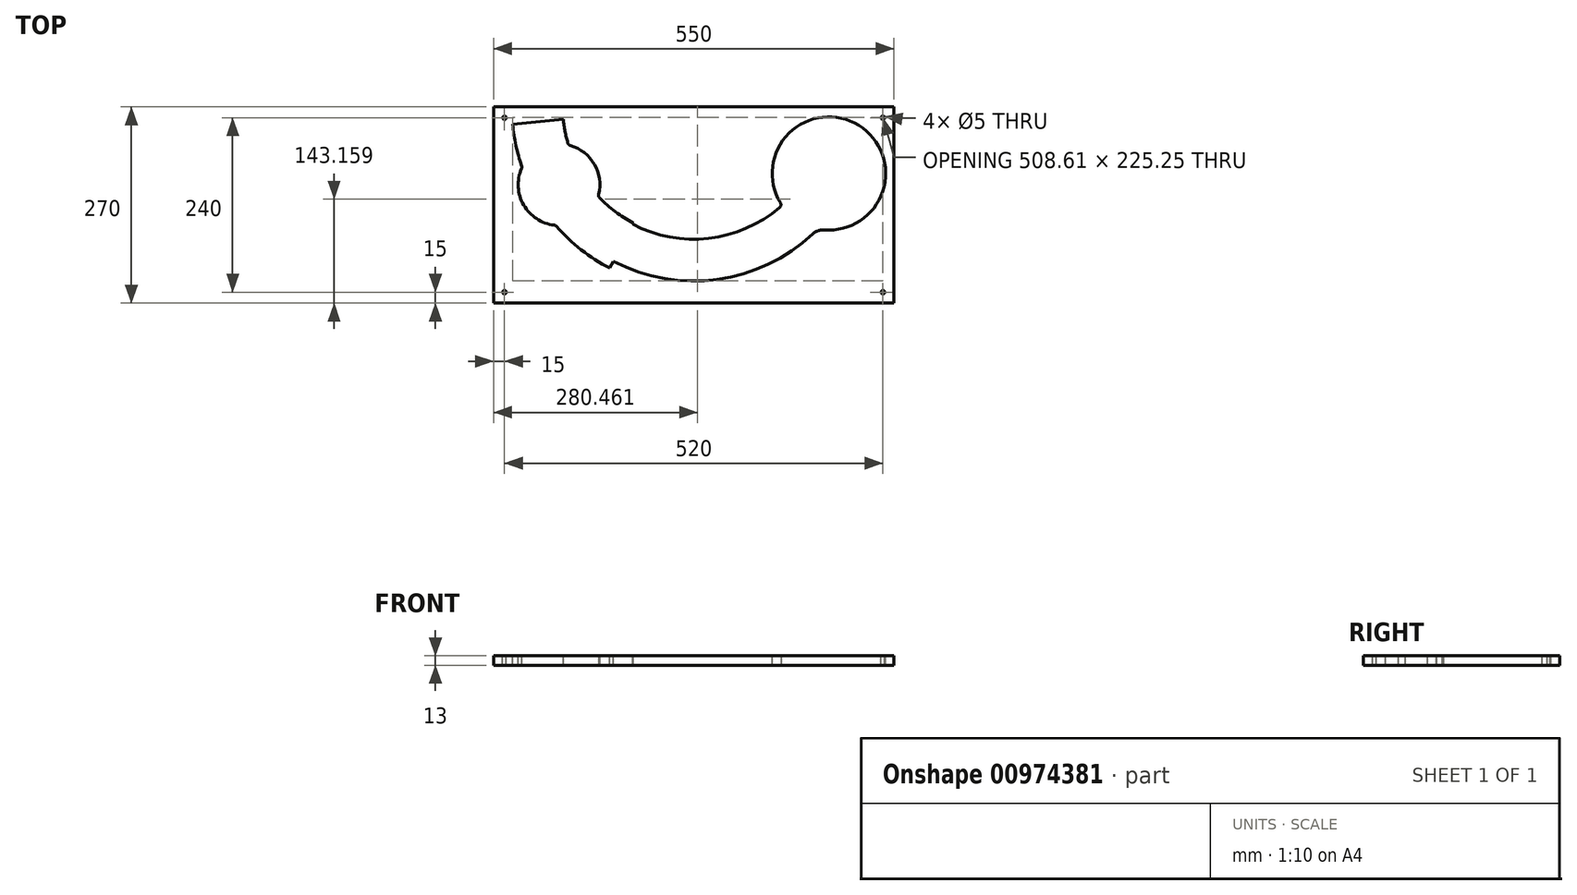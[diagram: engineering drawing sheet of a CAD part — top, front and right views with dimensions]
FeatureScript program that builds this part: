
annotation { "Feature Type Name" : "Feature", "Feature Type Description" : "" }
export const myFeature = defineFeature(function(context is Context, id is Id, definition is map)
    precondition{}
    {
        {
            var Q0;
            Q0=qCreatedBy(makeId("Top.planeOp"),FACE);
            var sketch = newSketch(context, id + "F0", { "sketchPlane" : qUnion([Q0])});
            skLineSegment(sketch, "E0.bottom", {"start": v(0, 0) * mm, "end": v(550, 0) * mm});
            skLineSegment(sketch, "E0.top", {"start": v(0, -270) * mm, "end": v(550, -270) * mm});
            skLineSegment(sketch, "E0.left", {"start": v(0, 0) * mm, "end": v(0, -270) * mm});
            skLineSegment(sketch, "E0.right", {"start": v(550, 0) * mm, "end": v(550, -270) * mm});
            skSolve(sketch);
        }
        {
            var Q0;
            Q0=makeQuery(id+"F0.imprint","IMPRINT",FACE,{"disambiguationData":[TD([[makeQuery(id+"F0.imprint","IMPRINT",EDGE,{"derivedFrom":sQuery(id+"F0.wireOp",EDGE,"E0.bottom")}),-1.0]])]});
            extrude(context, id + "F1", {"entities" : qUnion([Q0]), "oppositeDirection" : true, "depth" : 13 * mm, "offsetDistance" : 25 * mm});
        }
        {
            var Q0;
            Q0=makeQuery(id+"F1.opExtrude","CAP_FACE",FACE,{"disambiguationData":[OSD([sQuery(id+"F0.wireOp",EDGE,"E0.bottom"),sQuery(id+"F0.wireOp",EDGE,"E0.top"),sQuery(id+"F0.wireOp",EDGE,"E0.left"),sQuery(id+"F0.wireOp",EDGE,"E0.right")])],"isStart":true});
            var sketch = newSketch(context, id + "F2", { "sketchPlane" : qUnion([Q0])});
            skArc(sketch, "E1", {"start": v(26.15, -24) * mm, "mid": v(195.26, -236.94) * mm, "end": v(458.7, -169.57) * mm});
            skArc(sketch, "E2", {"start": v(95.83, -17.28) * mm, "mid": v(209.67, -167.73) * mm, "end": v(395.28, -133.91) * mm});
            skPoint(sketch, "E3.start.orphan", {"position": v(275, -180) * mm});
            skCircle(sketch, "E4", {"center": v(460.77, -91.66) * mm, "radius": 77.94 * mm});
            skLineSegment(sketch, "E5", {"start": v(95.83, -17.28) * mm, "end": v(26.15, -24) * mm});
            skLineSegment(sketch, "E6", {"start": v(191.91, -159.67) * mm, "end": v(159.6, -221.77) * mm});
            skLineSegment(sketch, "E7", {"start": v(550, 0) * mm, "end": v(535, 0) * mm});
            skLineSegment(sketch, "E8", {"start": v(535, 0) * mm, "end": v(535, -15) * mm});
            skLineSegment(sketch, "E9", {"start": v(0, -270) * mm, "end": v(15, -270) * mm});
            skLineSegment(sketch, "E10", {"start": v(15, -270) * mm, "end": v(15, -255) * mm});
            skCircle(sketch, "E11", {"center": v(15, -255) * mm, "radius": 2.5 * mm});
            skCircle(sketch, "E12", {"center": v(535, -255) * mm, "radius": 2.5 * mm});
            skCircle(sketch, "E13", {"center": v(535, -15) * mm, "radius": 2.5 * mm});
            skCircle(sketch, "E14", {"center": v(15, -15) * mm, "radius": 2.5 * mm});
            skCircle(sketch, "E15", {"center": v(89.9, -107.02) * mm, "radius": 56.06 * mm});
            skCircle(sketch, "E16", {"center": v(275, 0) * mm, "radius": 182 * mm});
            skCircle(sketch, "E17", {"center": v(275, 0) * mm, "radius": 239.5 * mm});
            skSolve(sketch);
        }
        {
            var Q0;
            {var subQ0=sQuery(id+"F2.wireOp",EDGE,"E15");var subQ1=sQuery(id+"F2.wireOp",EDGE,"E2");var subQ2=makeQuery(id+"F2.imprint","INTERSECT",VERTEX,{"disambiguationData":[OD(0.0)],"derivedFrom":[subQ1,subQ0]});Q0=makeQuery(id+"F2.imprint","IMPRINT",FACE,{"disambiguationData":[TD([[makeQuery(id+"F2.imprint","IMPRINT",EDGE,{"disambiguationData":[TD([[subQ2,-1.0]])],"derivedFrom":subQ1}),1.0]])]});}
            var Q1;
            {var subQ0=sQuery(id+"F2.wireOp",EDGE,"E16");var subQ1=sQuery(id+"F2.wireOp",EDGE,"E15");var subQ2=makeQuery(id+"F2.imprint","INTERSECT",VERTEX,{"disambiguationData":[OD(0.0)],"derivedFrom":[subQ1,subQ0]});Q1=makeQuery(id+"F2.imprint","IMPRINT",FACE,{"disambiguationData":[TD([[makeQuery(id+"F2.imprint","IMPRINT",EDGE,{"disambiguationData":[TD([[subQ2,-1.0]])],"derivedFrom":subQ1}),1.0]])]});}
            var Q2;
            {var subQ0=sQuery(id+"F2.wireOp",EDGE,"E16");var subQ1=sQuery(id+"F2.wireOp",EDGE,"E5");var subQ2=makeQuery(id+"F2.imprint","INTERSECT",VERTEX,{"derivedFrom":[subQ1,subQ0]});Q2=makeQuery(id+"F2.imprint","IMPRINT",FACE,{"disambiguationData":[TD([[makeQuery(id+"F2.imprint","IMPRINT",EDGE,{"disambiguationData":[TD([[subQ2,-1.0]])],"derivedFrom":subQ1}),1.0]])]});}
            var Q3;
            {var subQ0=sQuery(id+"F2.wireOp",EDGE,"E5");var subQ1=sQuery(id+"F2.wireOp",EDGE,"E1");var subQ2=makeQuery(id+"F2.imprint","INTERSECT",VERTEX,{"derivedFrom":[subQ1,subQ0]});Q3=makeQuery(id+"F2.imprint","IMPRINT",FACE,{"disambiguationData":[TD([[makeQuery(id+"F2.imprint","IMPRINT",EDGE,{"disambiguationData":[TD([[subQ2,-1.0]])],"derivedFrom":subQ1}),1.0]])]});}
            var Q4;
            {var subQ0=sQuery(id+"F2.wireOp",EDGE,"E15");var subQ1=sQuery(id+"F2.wireOp",EDGE,"E1");var subQ2=makeQuery(id+"F2.imprint","INTERSECT",VERTEX,{"disambiguationData":[OD(0.0)],"derivedFrom":[subQ1,subQ0]});Q4=makeQuery(id+"F2.imprint","IMPRINT",FACE,{"disambiguationData":[TD([[makeQuery(id+"F2.imprint","IMPRINT",EDGE,{"disambiguationData":[TD([[subQ2,-1.0]])],"derivedFrom":subQ1}),1.0]])]});}
            var Q5;
            {var subQ0=sQuery(id+"F2.wireOp",EDGE,"E15");var subQ1=sQuery(id+"F2.wireOp",EDGE,"E1");var subQ2=makeQuery(id+"F2.imprint","INTERSECT",VERTEX,{"disambiguationData":[OD(0.0)],"derivedFrom":[subQ1,subQ0]});Q5=makeQuery(id+"F2.imprint","IMPRINT",FACE,{"disambiguationData":[TD([[makeQuery(id+"F2.imprint","IMPRINT",EDGE,{"disambiguationData":[TD([[subQ2,-1.0]])],"derivedFrom":subQ1}),-1.0]])]});}
            var Q6;
            {var subQ0=sQuery(id+"F2.wireOp",EDGE,"E16");var subQ1=sQuery(id+"F2.wireOp",EDGE,"E6");var subQ2=makeQuery(id+"F2.imprint","INTERSECT",VERTEX,{"derivedFrom":[subQ1,subQ0]});Q6=makeQuery(id+"F2.imprint","IMPRINT",FACE,{"disambiguationData":[TD([[makeQuery(id+"F2.imprint","IMPRINT",EDGE,{"disambiguationData":[TD([[subQ2,-1.0]])],"derivedFrom":subQ1}),-1.0]])]});}
            var Q7;
            {var subQ0=sQuery(id+"F2.wireOp",EDGE,"E6");var subQ1=sQuery(id+"F2.wireOp",EDGE,"E1");var subQ2=makeQuery(id+"F2.imprint","INTERSECT",VERTEX,{"derivedFrom":[subQ1,subQ0]});Q7=makeQuery(id+"F2.imprint","IMPRINT",FACE,{"disambiguationData":[TD([[makeQuery(id+"F2.imprint","IMPRINT",EDGE,{"disambiguationData":[TD([[subQ2,1.0]])],"derivedFrom":subQ1}),1.0]])]});}
            var Q8;
            {var subQ0=sQuery(id+"F2.wireOp",EDGE,"E6");var subQ1=sQuery(id+"F2.wireOp",EDGE,"E2");var subQ2=makeQuery(id+"F2.imprint","INTERSECT",VERTEX,{"derivedFrom":[subQ1,subQ0]});Q8=makeQuery(id+"F2.imprint","IMPRINT",FACE,{"disambiguationData":[TD([[makeQuery(id+"F2.imprint","IMPRINT",EDGE,{"disambiguationData":[TD([[subQ2,1.0]])],"derivedFrom":subQ1}),-1.0]])]});}
            var Q9;
            {var subQ0=sQuery(id+"F2.wireOp",EDGE,"E16");var subQ1=sQuery(id+"F2.wireOp",EDGE,"E4");var subQ2=makeQuery(id+"F2.imprint","INTERSECT",VERTEX,{"disambiguationData":[OD(1.0)],"derivedFrom":[subQ1,subQ0]});Q9=makeQuery(id+"F2.imprint","IMPRINT",FACE,{"disambiguationData":[TD([[makeQuery(id+"F2.imprint","IMPRINT",EDGE,{"disambiguationData":[TD([[subQ2,-1.0]])],"derivedFrom":subQ1}),-1.0]])]});}
            var Q10;
            {var subQ0=sQuery(id+"F2.wireOp",EDGE,"E16");var subQ1=sQuery(id+"F2.wireOp",EDGE,"E4");var subQ2=makeQuery(id+"F2.imprint","INTERSECT",VERTEX,{"disambiguationData":[OD(0.0)],"derivedFrom":[subQ1,subQ0]});Q10=makeQuery(id+"F2.imprint","IMPRINT",FACE,{"disambiguationData":[TD([[makeQuery(id+"F2.imprint","IMPRINT",EDGE,{"disambiguationData":[TD([[subQ2,1.0]])],"derivedFrom":subQ1}),1.0]])]});}
            var Q11;
            {var subQ0=sQuery(id+"F2.wireOp",EDGE,"E4");var subQ1=makeQuery(id+"F2.imprint","INTERSECT",VERTEX,{"derivedFrom":[sQuery(id+"F2.wireOp",EDGE,"E2"),subQ0]});Q11=makeQuery(id+"F2.imprint","IMPRINT",FACE,{"disambiguationData":[TD([[makeQuery(id+"F2.imprint","IMPRINT",EDGE,{"disambiguationData":[TD([[subQ1,1.0]])],"derivedFrom":subQ0}),1.0]])]});}
            var Q12;
            {var subQ0=sQuery(id+"F2.wireOp",EDGE,"E4");var subQ1=makeQuery(id+"F2.imprint","INTERSECT",VERTEX,{"derivedFrom":[sQuery(id+"F2.wireOp",EDGE,"E1"),subQ0]});Q12=makeQuery(id+"F2.imprint","IMPRINT",FACE,{"disambiguationData":[TD([[makeQuery(id+"F2.imprint","IMPRINT",EDGE,{"disambiguationData":[TD([[subQ1,1.0]])],"derivedFrom":subQ0}),1.0]])]});}
            var Q13;
            Q13=makeQuery(id+"F2.imprint","IMPRINT",FACE,{"disambiguationData":[TD([[makeQuery(id+"F2.imprint","IMPRINT",EDGE,{"derivedFrom":sQuery(id+"F2.wireOp",EDGE,"E11")}),1.0]])]});
            var Q14;
            Q14=makeQuery(id+"F2.imprint","IMPRINT",FACE,{"disambiguationData":[TD([[makeQuery(id+"F2.imprint","IMPRINT",EDGE,{"derivedFrom":sQuery(id+"F2.wireOp",EDGE,"E14")}),1.0]])]});
            var Q15;
            Q15=makeQuery(id+"F2.imprint","IMPRINT",FACE,{"disambiguationData":[TD([[makeQuery(id+"F2.imprint","IMPRINT",EDGE,{"derivedFrom":sQuery(id+"F2.wireOp",EDGE,"E13")}),1.0]])]});
            var Q16;
            Q16=makeQuery(id+"F2.imprint","IMPRINT",FACE,{"disambiguationData":[TD([[makeQuery(id+"F2.imprint","IMPRINT",EDGE,{"derivedFrom":sQuery(id+"F2.wireOp",EDGE,"E12")}),1.0]])]});
            var Q17;
            {var subQ0=sQuery(id+"F2.wireOp",EDGE,"E15");var subQ1=sQuery(id+"F2.wireOp",EDGE,"E2");var subQ2=makeQuery(id+"F2.imprint","INTERSECT",VERTEX,{"disambiguationData":[OD(0.0)],"derivedFrom":[subQ1,subQ0]});Q17=makeQuery(id+"F2.imprint","IMPRINT",FACE,{"disambiguationData":[TD([[makeQuery(id+"F2.imprint","IMPRINT",EDGE,{"disambiguationData":[TD([[subQ2,-1.0]])],"derivedFrom":subQ1}),-1.0]])]});}
            var Q18;
            {var subQ0=sQuery(id+"F2.wireOp",EDGE,"E5");var subQ1=sQuery(id+"F2.wireOp",EDGE,"E2");var subQ2=makeQuery(id+"F2.imprint","INTERSECT",VERTEX,{"derivedFrom":[subQ1,subQ0]});Q18=makeQuery(id+"F2.imprint","IMPRINT",FACE,{"disambiguationData":[TD([[makeQuery(id+"F2.imprint","IMPRINT",EDGE,{"disambiguationData":[TD([[subQ2,-1.0]])],"derivedFrom":subQ1}),-1.0]])]});}
            extrude(context, id + "F3", {"entities" : qUnion([Q0, Q1, Q2, Q3, Q4, Q5, Q6, Q7, Q8, Q9, Q10, Q11, Q12, Q13, Q14, Q15, Q16, Q17, Q18]), "operationType" : NewBodyOperationType.REMOVE, "oppositeDirection" : true, "depth" : 25 * mm, "offsetDistance" : 25 * mm});
        }
        {
            var Q0;
            Q0=makeQuery(id+"F3.boolean.opBoolean","COPY",EDGE,{"derivedFrom":makeQuery(id+"F3.opExtrude","SWEPT_EDGE",EDGE,{"disambiguationData":[OSD([sQuery(id+"F2.wireOp",EDGE,"E2"),sQuery(id+"F2.wireOp",EDGE,"E15")])]})});
            var Q1;
            {var subQ0=sQuery(id+"F2.wireOp",EDGE,"E15");var subQ1=sQuery(id+"F2.wireOp",EDGE,"E1");Q1=makeQuery(id+"F3.boolean.opBoolean","COPY",EDGE,{"derivedFrom":makeQuery(id+"F3.opExtrude","SWEPT_EDGE",EDGE,{"disambiguationData":[OSD([subQ1,subQ0]),TDD([makeQuery(id+"F2.imprint","INTERSECT",VERTEX,{"disambiguationData":[OD(0.0)],"derivedFrom":[subQ1,subQ0]})])]})});}
            var Q2;
            {var subQ0=sQuery(id+"F2.wireOp",EDGE,"E15");var subQ1=sQuery(id+"F2.wireOp",EDGE,"E1");Q2=makeQuery(id+"F3.boolean.opBoolean","COPY",EDGE,{"derivedFrom":makeQuery(id+"F3.opExtrude","SWEPT_EDGE",EDGE,{"disambiguationData":[OSD([subQ1,subQ0]),TDD([makeQuery(id+"F2.imprint","INTERSECT",VERTEX,{"disambiguationData":[OD(1.0)],"derivedFrom":[subQ1,subQ0]})])]})});}
            var Q3;
            {var subQ0=sQuery(id+"F2.wireOp",EDGE,"E15");var subQ1=sQuery(id+"F2.wireOp",EDGE,"E1");Q3=makeQuery(id+"F3.boolean.opBoolean","COPY",EDGE,{"derivedFrom":makeQuery(id+"F3.opExtrude","SWEPT_EDGE",EDGE,{"disambiguationData":[OSD([subQ1,subQ0]),TDD([makeQuery(id+"F2.imprint","INTERSECT",VERTEX,{"disambiguationData":[OD(0.0)],"derivedFrom":[subQ1,subQ0]})])]})});}
            var Q4;
            {var subQ0=sQuery(id+"F2.wireOp",EDGE,"E15");var subQ1=sQuery(id+"F2.wireOp",EDGE,"E1");Q4=makeQuery(id+"F3.boolean.opBoolean","COPY",EDGE,{"derivedFrom":makeQuery(id+"F3.opExtrude","SWEPT_EDGE",EDGE,{"disambiguationData":[OSD([subQ1,subQ0]),TDD([makeQuery(id+"F2.imprint","INTERSECT",VERTEX,{"disambiguationData":[OD(1.0)],"derivedFrom":[subQ1,subQ0]})])]})});}
            var Q5;
            {var subQ0=sQuery(id+"F2.wireOp",EDGE,"E15");var subQ1=sQuery(id+"F2.wireOp",EDGE,"E2");Q5=makeQuery(id+"F3.boolean.opBoolean","COPY",EDGE,{"derivedFrom":makeQuery(id+"F3.opExtrude","SWEPT_EDGE",EDGE,{"disambiguationData":[OSD([subQ1,subQ0]),TDD([makeQuery(id+"F2.imprint","INTERSECT",VERTEX,{"disambiguationData":[OD(0.0)],"derivedFrom":[subQ1,subQ0]})])]})});}
            var Q6;
            {var subQ0=sQuery(id+"F2.wireOp",EDGE,"E15");var subQ1=sQuery(id+"F2.wireOp",EDGE,"E2");Q6=makeQuery(id+"F3.boolean.opBoolean","COPY",EDGE,{"derivedFrom":makeQuery(id+"F3.opExtrude","SWEPT_EDGE",EDGE,{"disambiguationData":[OSD([subQ1,subQ0]),TDD([makeQuery(id+"F2.imprint","INTERSECT",VERTEX,{"disambiguationData":[OD(1.0)],"derivedFrom":[subQ1,subQ0]})])]})});}
            var Q7;
            Q7=makeQuery(id+"F3.boolean.opBoolean","COPY",EDGE,{"derivedFrom":makeQuery(id+"F3.opExtrude","SWEPT_EDGE",EDGE,{"disambiguationData":[OSD([sQuery(id+"F2.wireOp",EDGE,"E4"),sQuery(id+"F2.wireOp",EDGE,"E16")])]})});
            fillet(context, id + "F4", {"entities" : qUnion([Q0, Q1, Q2, Q3, Q4, Q5, Q6, Q7]), "radius" : 5 * mm, "tangentPropagation" : true, "allowEdgeOverflow" : false});
        }
        {
            var Q0;
            Q0=makeQuery(id+"F3.boolean.opBoolean","COPY",EDGE,{"derivedFrom":makeQuery(id+"F3.opExtrude","SWEPT_EDGE",EDGE,{"disambiguationData":[OSD([sQuery(id+"F2.wireOp",EDGE,"E4"),sQuery(id+"F2.wireOp",EDGE,"E16")])]})});
            var Q1;
            Q1=makeQuery(id+"F3.boolean.opBoolean","COPY",EDGE,{"derivedFrom":makeQuery(id+"F3.opExtrude","SWEPT_EDGE",EDGE,{"disambiguationData":[OSD([sQuery(id+"F2.wireOp",EDGE,"E4"),sQuery(id+"F2.wireOp",EDGE,"E17")])]})});
            fillet(context, id + "F5", {"entities" : qUnion([Q0, Q1]), "radius" : 20 * mm, "tangentPropagation" : true, "allowEdgeOverflow" : false});
        }
    });
